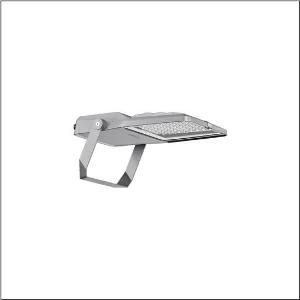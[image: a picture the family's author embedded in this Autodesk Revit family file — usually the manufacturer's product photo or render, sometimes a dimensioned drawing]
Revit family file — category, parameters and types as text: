
# Revit family: floodlight_fl_21_iq_mini___pl43_5xa7772b1a1a_21a9
name_source: partatom
category: Lighting Fixtures
units: mm (PartAtom-declared; Revit-internal decimal feet)

## family parameters
Cut with Voids When Loaded = No
Host = Face
Light Source = No
Part Type = Normal
Room Calculation Point = No
Round Connector Dimension = Use Diameter
Shared = No

## types (1)
- --- (1 x LED, 5300 lm, 45.5 W, 2200K)
    Apparent Load = 46 VA
    CIE Flux Codes = 27 78 99 100 100
    Color Rendering = 70
    Color Temperature = 2200K
    Default Elevation = 1800 mm
    Description = Floodlight FL 21 iQ mini, floodlight, primary light control with lens, of PMMA, primary optical cover: protective disc, of toughened safety glass, transparent, light distribution: PL43, light emission: direct distribution, installation type: surface-mounted, lamps: LED, High Power LED, rated values: 5.300lm | 45,5W | 116,5lm/W (begin service life); end service life: 5.300lm | 48W; at 50% lumin. flux: 2.650lm | 21,4W | 123,8lm/W, colour temperature: 2200K, colour rendering: CRI > 70, light colour: 722, light setting 1 begin service life: 100% | 5.300lm | 45,5W | 116,5lm/W | 2.200K, light setting 1 end service life: 48W, further light settings possible, control: Street-Remote, Auto-Match, Temp-Guard, Night-Set, Smart-Wire, Desk-Remote (wireless, voltage-free reading and setting of iQ features in the workshop via application-optimized NFC function/RFID function), optimised constant luminous flux control (CLO 2.0), pre-setting: linear dimming characteristic, with terminal, 6-pole, mains connection: 220..240V, AC, 50/60Hz, luminaire housing, of diecast aluminium, powder-coated, SITECO metallic grey (DB 702S), corrosivity category C5 mid according to DIN EN ISO 12944suitable for swimming poolschlorine-resistant, sealing non-destructively replaceable, mounting bracket, of steel, galvanised, powder-coated, SITECO metallic grey (DB 702S), protection rating (complete): IP66, insulation class (complete): insulation class II (safety insulation), certification: CE, ENEC, VDE, protection symbol: D, impact resistance: IK08, permissible operating ambient temperature: -40..+40°C, permissible operating ambient temperature for outdoor applications: -40..+50°C, standard: DIN EN 12944, LABS conformity tested according to VDMA 24364:2018-05, packaging unit: 1 piece

Light Distribution: PL43
    Height = 70 mm
    Lamp = 1 x LED
    Lamp Light Flux = 5300 lm
    Lamp Power = 45.5 W
    Lamp count = 1
    Length = 485 mm
    Luminous efficacy = 116 lm/W
    Manufacturer = Siteco
    ModVariant = No
    Model = 5XA7772B1A1A
    Mounting Place = Pole
    Mounting Type = Pole annexe
    Number of Poles = 1
    OnlyDefault = Yes
    Power Factor = 1
    Product Name = Floodlight FL 21 iQ mini | PL43
    Product group = floodlight | pylon annexe
    ProductGroupID = 6201
    Protection Class = Protection class II
    Protection Degree = IP 66
    RLX_Detail_Level = 1
    RLX_Emergency_Light_Flux = 0 lm
    RLX_Emergency_Type = 0
    RLX_Emergency_Type_DB = No
    RlxData = <blob elided: 96309 chars, md5=263ec086>
    Socket = socket
    Standby Power = 0 W
    System Light Flux = 5300 lm
    System Power = 46 W
    Type Comments = factory setting: luminous flux: 100 % | dim-lin: 254 | 463 mA
    Type Image = l_1006845.jpg
    URL = http://relux.com
    VarID = @adj_163879
    Voltage = 0 V
    Weight = 0.00 kg
    Width = 337 mm

## geometry (parser evidence)
native form markers: Blend x4, Sweep x11
no freeform markers — native parametric forms only
